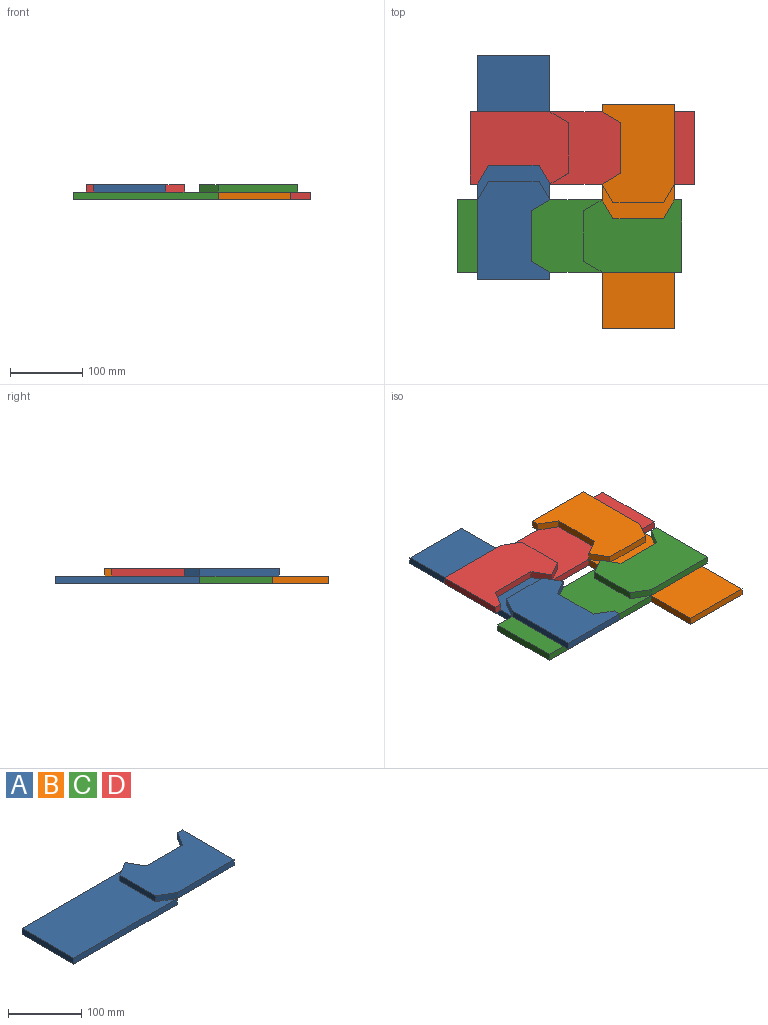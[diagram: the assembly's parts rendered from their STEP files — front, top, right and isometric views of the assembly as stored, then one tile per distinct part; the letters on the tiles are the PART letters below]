
ASSEMBLY  parts=4 mates=7
PART A: 17 faces, bbox 310x100x20 mm
  f0: plane 26x15mm, normal (-0.5,0.87,0), area 300.2mm2, adj f1,f8,f9,f11
  f1: plane 70x10mm, normal (-1,0,0), area 700mm2, adj f0,f2,f9,f11
  f2: plane 26x15mm, normal (-0.5,-0.87,0), area 300.2mm2, adj f1,f3,f9,f11
  f3: plane 110x10mm, normal (0,-1,0), area 1100mm2, adj f2,f4,f9,f10
  f4: plane 100x10mm, normal (1,0,0), area 1000mm2, adj f3,f5,f9,f10
  f5: plane 10x10mm, normal (0,1,0), area 100mm2, adj f4,f6,f9,f10
  f6: plane 26x15mm, normal (-0.87,0.5,0), area 300.2mm2, adj f5,f7,f9,f10
  f7: plane 70x10mm, normal (0,1,0), area 700mm2, adj f6,f8,f9,f10
  f8: plane 26x15mm, normal (0.87,0.5,0), area 300.2mm2, adj f0,f7,f9,f10
  f9: plane 136x100mm, normal (0,0,1), area 11000mm2, adj f0,f1,f2,f3,f4,f5,f6,f7
  f10: plane 110x100mm, normal (0,0,-1), area 8790mm2, adj f3,f4,f5,f6,f7,f8,f13
  f11: plane 200x100mm, normal (0,0,1), area 17790mm2, adj f0,f1,f2,f12,f14,f15
  f12: plane 200x10mm, normal (0,1,0), area 2000mm2, adj f11,f13,f15,f16
  f13: plane 100x10mm, normal (1,0,0), area 1000mm2, adj f10,f12,f14,f16
  f14: plane 200x10mm, normal (0,-1,0), area 2000mm2, adj f11,f13,f15,f16
  f15: plane 100x10mm, normal (-1,0,0), area 1000mm2, adj f11,f12,f14,f16
  f16: plane 200x100mm, normal (0,0,-1), area 20000mm2, adj f12,f13,f14,f15
PART B: same geometry as A
PART C: same geometry as A
PART D: same geometry as A
PLACE A rot(axis=(0,0,-1),90deg) t=(-168.44,-135.19,-119.34)mm
PLACE B rot(axis=(0,0,1),90deg) t=(103.85,-113.15,-119.34)mm fixed
PLACE C t=(3.85,-235.19,-119.34)mm
PLACE D rot(axis=(0,0,-1),180deg) t=(-68.44,-13.15,-119.34)mm
MATE planar A.f11 <-> D.f10  axis (0,0,1) through (-118.44,-24.29,-119.34)mm
MATE planar B.f12 <-> C.f13  axis (-1,0,0) through (3.85,-213.15,-124.34)mm
MATE planar B.f10 <-> D.f11  axis (0,0,-1) through (63.34,-56.89,-119.34)mm
MATE planar A.f13 <-> C.f12  axis (0,-1,0) through (-118.44,-135.19,-124.34)mm
MATE planar D.f12 <-> B.f13  axis (0,-1,0) through (31.56,-113.15,-124.34)mm
MATE planar B.f10 <-> C.f11  axis (0,0,-1) through (63.34,-56.89,-119.34)mm
MATE planar A.f12 <-> D.f13  axis (1,0,0) through (-68.44,-35.19,-124.34)mm
